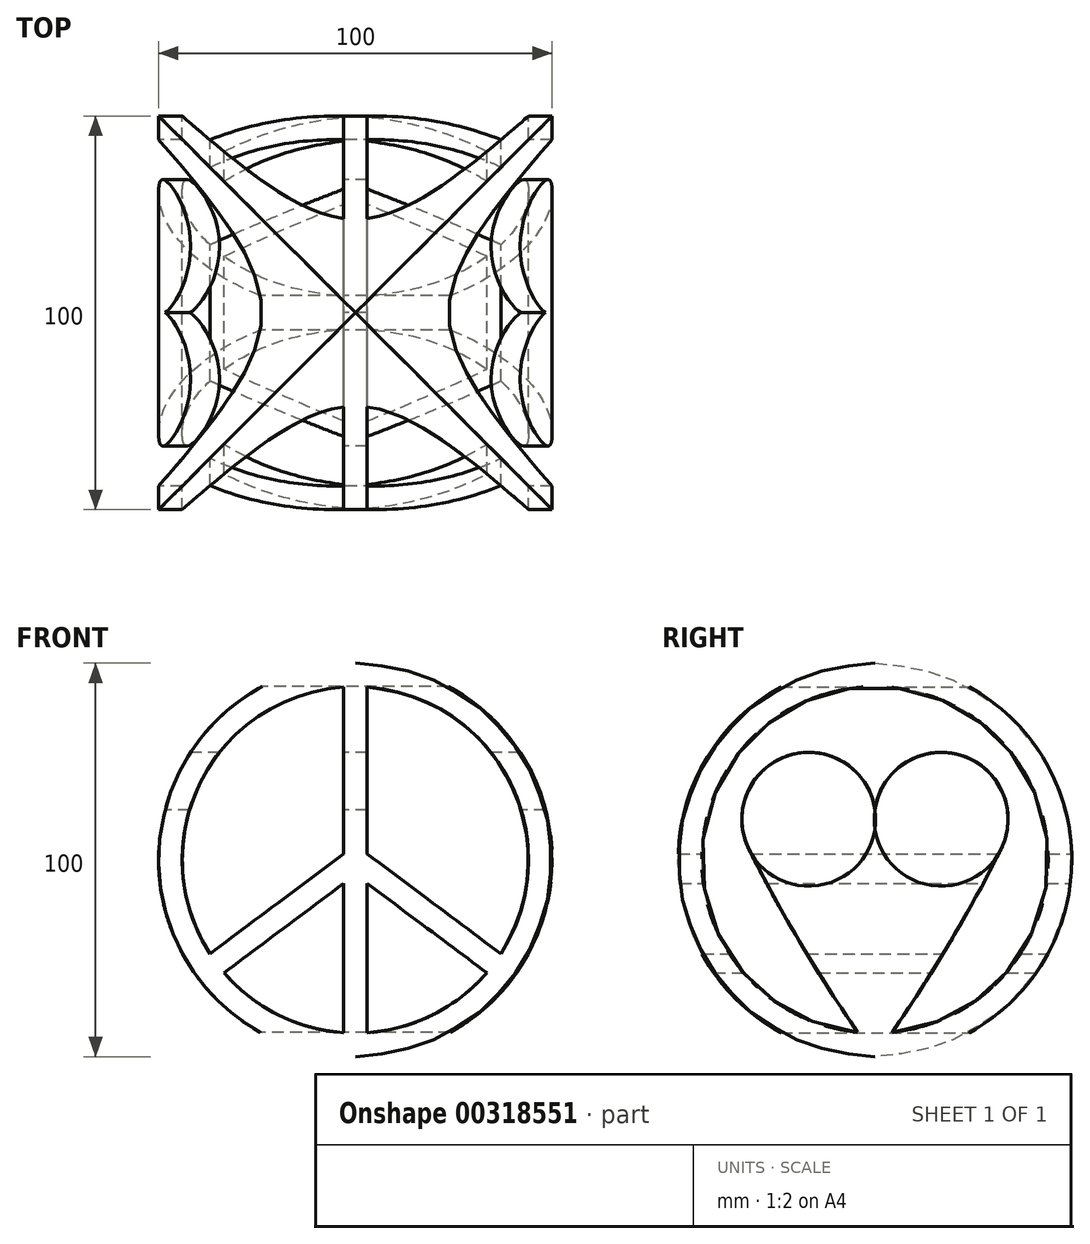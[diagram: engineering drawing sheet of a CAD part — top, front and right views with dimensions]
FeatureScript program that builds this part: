
annotation { "Feature Type Name" : "Feature", "Feature Type Description" : "" }
export const myFeature = defineFeature(function(context is Context, id is Id, definition is map)
    precondition{}
    {
        {
            var Q0;
            Q0=qCreatedBy(makeId("Front.planeOp"),FACE);
            var sketch = newSketch(context, id + "F0", { "sketchPlane" : qUnion([Q0])});
            skCircle(sketch, "E0", {"center": v(0, 0) * mm, "radius": 50 * mm});
            skArc(sketch, "E1.0", {"start": v(-33.38, -28.66) * mm, "mid": v(-19.72, -39.33) * mm, "end": v(-3, -43.9) * mm});
            skLineSegment(sketch, "E2", {"start": v(0, 44) * mm, "end": v(0, 0) * mm, "construction": true});
            skLineSegment(sketch, "E3", {"start": v(0, 0) * mm, "end": v(0, -44) * mm, "construction": true});
            skLineSegment(sketch, "E4", {"start": v(0, -44) * mm, "end": v(0, 0) * mm, "construction": true});
            skLineSegment(sketch, "E5", {"start": v(0, 0) * mm, "end": v(35.26, -26.32) * mm, "construction": true});
            skLineSegment(sketch, "E6.MirrorCS", {"start": v(0, 0) * mm, "end": v(-35.26, -26.32) * mm, "construction": true});
            skLineSegment(sketch, "E7.0.left", {"start": v(3, 44) * mm, "end": v(3, 1.5) * mm});
            skLineSegment(sketch, "E7.0.right", {"start": v(-3, 44) * mm, "end": v(-3, 1.5) * mm});
            skLineSegment(sketch, "E7.1.left", {"start": v(-3, -44) * mm, "end": v(-3, -5.98) * mm});
            skLineSegment(sketch, "E7.1.right", {"start": v(3, -44) * mm, "end": v(3, -5.98) * mm});
            skLineSegment(sketch, "E7.2.right", {"start": v(-3, 1.5) * mm, "end": v(-37.05, -23.92) * mm});
            skLineSegment(sketch, "E7.3.left", {"start": v(3, 1.5) * mm, "end": v(37.05, -23.92) * mm});
            skLineSegment(sketch, "E8.trimOffspring", {"start": v(-3, -5.98) * mm, "end": v(-33.46, -28.73) * mm});
            skLineSegment(sketch, "E9.trimOffspring", {"start": v(3, -5.98) * mm, "end": v(33.46, -28.73) * mm});
            skArc(sketch, "E10.trimOffspring", {"start": v(3, -43.9) * mm, "mid": v(19.72, -39.33) * mm, "end": v(33.38, -28.66) * mm});
            skArc(sketch, "E11.trimOffspring", {"start": v(36.97, -23.86) * mm, "mid": v(39.33, 19.72) * mm, "end": v(3, 43.9) * mm});
            skArc(sketch, "E12.trimOffspring", {"start": v(-3, 43.9) * mm, "mid": v(-39.33, 19.72) * mm, "end": v(-36.97, -23.86) * mm});
            skSolve(sketch);
        }
        {
            var Q0;
            Q0=qCreatedBy(makeId("Right.planeOp"),FACE);
            var sketch = newSketch(context, id + "F1", { "sketchPlane" : qUnion([Q0])});
            skCircle(sketch, "E13", {"center": v(0, 0) * mm, "radius": 50 * mm});
            skArc(sketch, "E14.0", {"start": v(4.4, -43.78) * mm, "mid": v(0, 44) * mm, "end": v(-4.4, -43.78) * mm});
            skArc(sketch, "E15", {"start": v(32, 2.66) * mm, "mid": v(21.94, 26.53) * mm, "end": v(0, 12.75) * mm});
            skArc(sketch, "E16", {"start": v(4.4, -43.78) * mm, "mid": v(19, -21.04) * mm, "end": v(32, 2.66) * mm});
            skArc(sketch, "E17.MirrorCS", {"start": v(-32, 2.66) * mm, "mid": v(-21.94, 26.53) * mm, "end": v(0, 12.75) * mm});
            skArc(sketch, "E18.MirrorCS", {"start": v(-4.4, -43.78) * mm, "mid": v(-19, -21.04) * mm, "end": v(-32, 2.66) * mm});
            skPoint(sketch, "E19.orphan", {"position": v(0, -50) * mm});
            skSolve(sketch);
        }
        {
            var Q0;
            {var subQ0=sQuery(id+"F1.wireOp",EDGE,"E13");Q0=makeQuery(id+"F1.imprint","IMPRINT",FACE,{"disambiguationData":[TD([[makeQuery(id+"F1.imprint","IMPRINT",EDGE,{"derivedFrom":subQ0}),1.0]])]});}
            var Q1;
            {var subQ1=sQuery(id+"F1.wireOp",EDGE,"E15");Q1=makeQuery(id+"F1.imprint","IMPRINT",FACE,{"disambiguationData":[TD([[makeQuery(id+"F1.imprint","IMPRINT",EDGE,{"derivedFrom":subQ1}),1.0]])]});}
            extrude(context, id + "F2", {"entities" : qUnion([Q0, Q1]), "endBound" : BoundingType.SYMMETRIC, "depth" : 100 * mm});
        }
        {
            var Q0;
            Q0=makeQuery(id+"F0.imprint","IMPRINT",FACE,{"disambiguationData":[TD([[makeQuery(id+"F0.imprint","IMPRINT",EDGE,{"derivedFrom":sQuery(id+"F0.wireOp",EDGE,"E0")}),1.0]])]});
            extrude(context, id + "F3", {"entities" : qUnion([Q0]), "operationType" : NewBodyOperationType.INTERSECT, "endBound" : BoundingType.SYMMETRIC, "depth" : 150 * mm});
        }
    });
